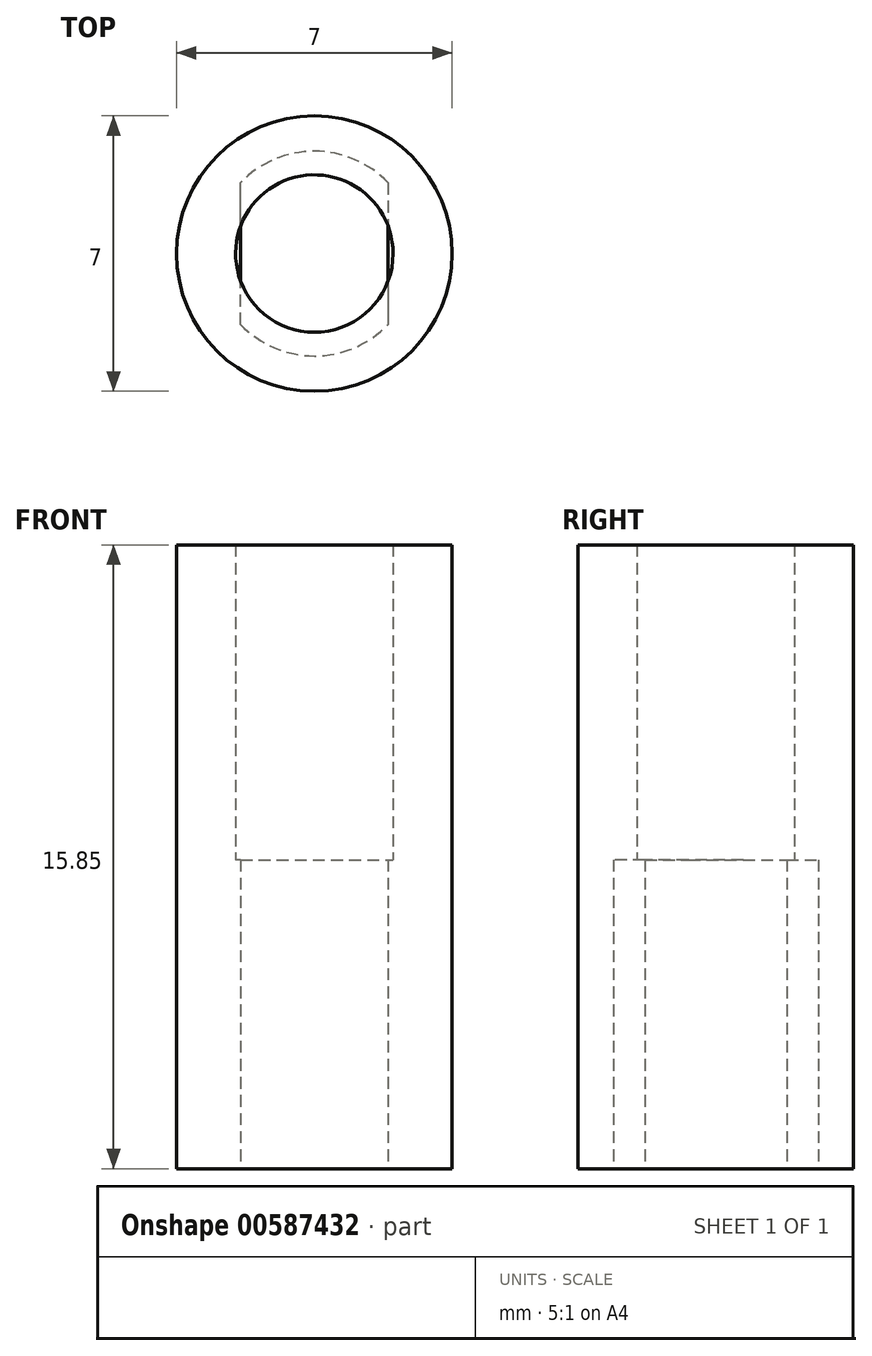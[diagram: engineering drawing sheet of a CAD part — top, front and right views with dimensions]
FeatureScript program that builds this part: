
annotation { "Feature Type Name" : "Feature", "Feature Type Description" : "" }
export const myFeature = defineFeature(function(context is Context, id is Id, definition is map)
    precondition{}
    {
        {
            var Q0;
            Q0=qCreatedBy(makeId("Top.planeOp"),FACE);
            var sketch = newSketch(context, id + "F0", { "sketchPlane" : qUnion([Q0])});
            skCircle(sketch, "E0", {"center": v(0, 0) * mm, "radius": 3.5 * mm});
            skCircle(sketch, "E1", {"center": v(0, 0) * mm, "radius": 2.6 * mm});
            skLineSegment(sketch, "E2", {"start": v(-1.87, -1.8) * mm, "end": v(-1.88, 1.8) * mm});
            skLineSegment(sketch, "E3", {"start": v(1.87, 1.8) * mm, "end": v(1.88, -1.8) * mm});
            skSolve(sketch);
        }
        {
            var Q0;
            Q0 = qSketchRegion(id + "F0", true);
            var Q1;
            {var subQ0=sQuery(id+"F0.wireOp",EDGE,"E3");Q1=makeQuery(id+"F0.imprint","IMPRINT",FACE,{"disambiguationData":[TD([[makeQuery(id+"F0.imprint","IMPRINT",EDGE,{"derivedFrom":subQ0}),1.0]])]});}
            var Q2;
            {var subQ0=sQuery(id+"F0.wireOp",EDGE,"E2");Q2=makeQuery(id+"F0.imprint","IMPRINT",FACE,{"disambiguationData":[TD([[makeQuery(id+"F0.imprint","IMPRINT",EDGE,{"derivedFrom":subQ0}),1.0]])]});}
            extrude(context, id + "F1", {"entities" : qUnion([Q0, Q1, Q2]), "depth" : 7.85 * mm, "offsetDistance" : 25 * mm});
        }
        {
            var Q0;
            Q0=makeQuery(id+"F1.opExtrude","CAP_FACE",FACE,{"disambiguationData":[OSD([sQuery(id+"F0.wireOp",EDGE,"E0"),sQuery(id+"F0.wireOp",EDGE,"E1"),sQuery(id+"F0.wireOp",EDGE,"E2"),sQuery(id+"F0.wireOp",EDGE,"E3")])],"isStart":false});
            var sketch = newSketch(context, id + "F2", { "sketchPlane" : qUnion([Q0])});
            skCircle(sketch, "E4", {"center": v(0, 0) * mm, "radius": 3.5 * mm});
            skCircle(sketch, "E5", {"center": v(0, 0) * mm, "radius": 2 * mm});
            skSolve(sketch);
        }
        {
            var Q0;
            Q0 = qSketchRegion(id + "F2", true);
            extrude(context, id + "F3", {"entities" : qUnion([Q0]), "operationType" : NewBodyOperationType.ADD, "depth" : 8 * mm, "offsetDistance" : 25 * mm});
        }
    });
